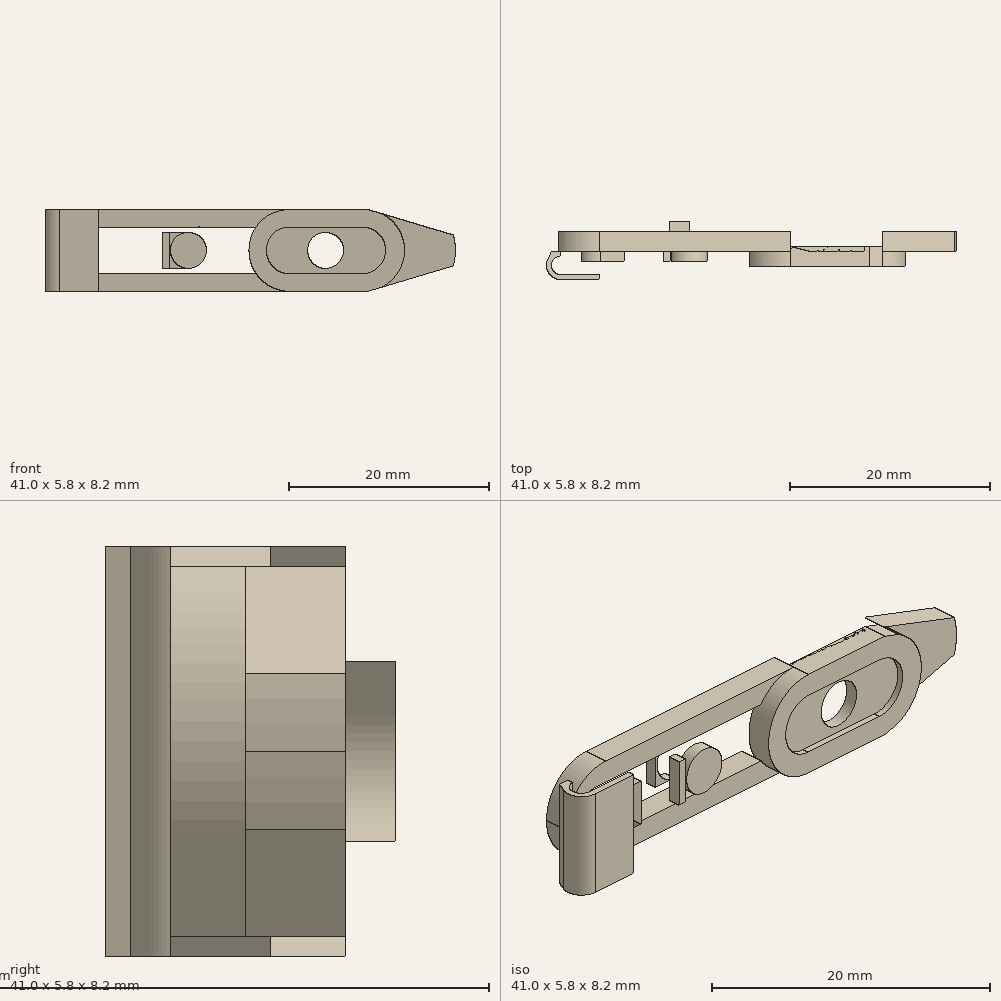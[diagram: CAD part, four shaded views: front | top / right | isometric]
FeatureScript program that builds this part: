
annotation { "Feature Type Name" : "Feature", "Feature Type Description" : "" }
export const myFeature = defineFeature(function(context is Context, id is Id, definition is map)
    precondition{}
    {
        {
            var Q0;
            Q0=qCreatedBy(makeId("Front.planeOp"),FACE);
            var sketch = newSketch(context, id + "F0", { "sketchPlane" : qUnion([Q0])});
            skLineSegment(sketch, "E0", {"start": v(24.15, -4.1) * mm, "end": v(24.15, 4.1) * mm});
            skLineSegment(sketch, "E1", {"start": v(24.15, 4.1) * mm, "end": v(-24.15, 4.1) * mm});
            skLineSegment(sketch, "E2", {"start": v(-24.15, 4.1) * mm, "end": v(-24.15, -4.1) * mm});
            skLineSegment(sketch, "E3", {"start": v(24.15, -4.1) * mm, "end": v(-24.15, -4.1) * mm});
            skLineSegment(sketch, "E4", {"start": v(-24.15, 0) * mm, "end": v(-24.15, 2.35) * mm});
            skLineSegment(sketch, "E5", {"start": v(-12.63, 2.35) * mm, "end": v(-1.7, 2.35) * mm});
            skLineSegment(sketch, "E6", {"start": v(7.64, 2.35) * mm, "end": v(14.81, 2.35) * mm});
            skLineSegment(sketch, "E7", {"start": v(-12.5, -2.35) * mm, "end": v(-1.7, -2.35) * mm});
            skLineSegment(sketch, "E8", {"start": v(7.5, -2.35) * mm, "end": v(14.81, -2.35) * mm});
            skArc(sketch, "E9", {"start": v(14.8, -0.1) * mm, "mid": v(14.9, 0) * mm, "end": v(14.8, 0.1) * mm});
            skArc(sketch, "E10", {"start": v(-12.63, 2.35) * mm, "mid": v(-14.91, -0.07) * mm, "end": v(-12.5, -2.35) * mm});
            skArc(sketch, "E11", {"start": v(14.85, 0.15) * mm, "mid": v(14.83, 0.16) * mm, "end": v(14.8, 0.16) * mm});
            skArc(sketch, "E12", {"start": v(14.96, 0) * mm, "mid": v(14.96, 0) * mm, "end": v(14.96, 0) * mm});
            skArc(sketch, "E13", {"start": v(14.8, -0.16) * mm, "mid": v(14.83, -0.16) * mm, "end": v(14.85, -0.15) * mm});
            skLineSegment(sketch, "E14", {"start": v(16.02, -3.91) * mm, "end": v(23.93, -1.56) * mm});
            skArc(sketch, "E15", {"start": v(23.66, -0.64) * mm, "mid": v(23.68, -0.62) * mm, "end": v(23.69, -0.6) * mm});
            skLineSegment(sketch, "E16", {"start": v(16.02, 3.91) * mm, "end": v(23.93, 1.56) * mm});
            skLineSegment(sketch, "E17", {"start": v(-14.84, 0) * mm, "end": v(-18.04, 0) * mm});
            skLineSegment(sketch, "E18", {"start": v(-13.4, -4) * mm, "end": v(-22.58, -1.95) * mm});
            skLineSegment(sketch, "E19", {"start": v(-22.58, -1.95) * mm, "end": v(-13.38, -4) * mm});
            skLineSegment(sketch, "E20", {"start": v(-22.48, 2.17) * mm, "end": v(-13.4, 4.01) * mm});
            skLineSegment(sketch, "E21", {"start": v(-13.02, 4.1) * mm, "end": v(-23.96, 1.87) * mm});
            skLineSegment(sketch, "E22", {"start": v(-12.94, -4.1) * mm, "end": v(-23.87, -1.67) * mm});
            skCircle(sketch, "E23", {"center": v(-11.6, 0) * mm, "radius": 1.8 * mm});
            skLineSegment(sketch, "E24", {"start": v(-14.84, 0) * mm, "end": v(0.66, 0) * mm});
            skArc(sketch, "E25", {"start": v(-1.42, -2.35) * mm, "mid": v(0.8, 0.14) * mm, "end": v(-1.7, 2.35) * mm});
            skLineSegment(sketch, "E26", {"start": v(0.66, 0) * mm, "end": v(-2.6, 0) * mm});
            skLineSegment(sketch, "E27", {"start": v(24.15, 0) * mm, "end": v(15.65, 0) * mm});
            skLineSegment(sketch, "E28", {"start": v(15.65, 0) * mm, "end": v(15.65, 0.9) * mm});
            skLineSegment(sketch, "E29", {"start": v(15.65, 0.9) * mm, "end": v(16.65, 0.9) * mm});
            skLineSegment(sketch, "E30", {"start": v(16.65, 0.9) * mm, "end": v(16.65, -0.9) * mm});
            skLineSegment(sketch, "E31", {"start": v(16.65, -0.9) * mm, "end": v(15.75, -0.9) * mm});
            skLineSegment(sketch, "E32", {"start": v(15.75, -0.9) * mm, "end": v(15.65, -0.9) * mm});
            skLineSegment(sketch, "E33", {"start": v(15.65, -0.9) * mm, "end": v(15.65, 0) * mm});
            skLineSegment(sketch, "E34", {"start": v(15.65, 0) * mm, "end": v(5.15, 0) * mm});
            skLineSegment(sketch, "E35", {"start": v(17.15, 0) * mm, "end": v(11.15, 0) * mm});
            skArc(sketch, "E36", {"start": v(11.85, -1.8) * mm, "mid": v(13.65, 0) * mm, "end": v(11.85, 1.8) * mm});
            skLineSegment(sketch, "E37", {"start": v(11.82, -0.07) * mm, "end": v(11.82, -0.07) * mm});
            skLineSegment(sketch, "E38", {"start": v(-24.15, 4.1) * mm, "end": v(-24.65, 4.1) * mm});
            skArc(sketch, "E39", {"start": v(-12.24, 1.8) * mm, "mid": v(-14.04, 0) * mm, "end": v(-12.24, -1.8) * mm});
            skArc(sketch, "E40", {"start": v(-1.95, -1.8) * mm, "mid": v(-0.15, 0) * mm, "end": v(-1.95, 1.8) * mm});
            skLineSegment(sketch, "E41", {"start": v(5.15, 0) * mm, "end": v(0.66, 0) * mm});
            skArc(sketch, "E42", {"start": v(7.64, 2.35) * mm, "mid": v(5.22, 0.07) * mm, "end": v(7.5, -2.35) * mm});
            skArc(sketch, "E43", {"start": v(14.81, -2.35) * mm, "mid": v(17.16, 0) * mm, "end": v(14.81, 2.35) * mm});
            skLineSegment(sketch, "E44", {"start": v(16.65, 0.9) * mm, "end": v(16.65, 1.45) * mm});
            skLineSegment(sketch, "E45", {"start": v(16.65, -0.9) * mm, "end": v(16.65, -1.45) * mm});
            skLineSegment(sketch, "E46", {"start": v(10.48, -0.07) * mm, "end": v(10.48, -0.07) * mm});
            skArc(sketch, "E47", {"start": v(10.45, 1.8) * mm, "mid": v(8.65, 0) * mm, "end": v(10.45, -1.8) * mm});
            skLineSegment(sketch, "E48", {"start": v(11.85, 1.8) * mm, "end": v(10.45, 1.8) * mm});
            skLineSegment(sketch, "E49", {"start": v(10.45, -1.8) * mm, "end": v(11.85, -1.8) * mm});
            skCircle(sketch, "E50", {"center": v(11.16, 0) * mm, "radius": 1.8 * mm});
            skLineSegment(sketch, "E51", {"start": v(-5.15, -1.8) * mm, "end": v(-5.15, 1.8) * mm});
            skArc(sketch, "E52", {"start": v(-1.95, -0.07) * mm, "mid": v(-1.88, 0) * mm, "end": v(-1.95, 0.07) * mm});
            skLineSegment(sketch, "E53", {"start": v(-1.95, 1.8) * mm, "end": v(-5.15, 1.8) * mm});
            skLineSegment(sketch, "E54", {"start": v(-1.95, -1.8) * mm, "end": v(-5.15, -1.8) * mm});
            skLineSegment(sketch, "E55", {"start": v(-4.54, -1.8) * mm, "end": v(-4.54, 1.8) * mm});
            skArc(sketch, "E56", {"start": v(-12.24, 0.07) * mm, "mid": v(-12.3, 0) * mm, "end": v(-12.24, -0.07) * mm});
            skLineSegment(sketch, "E57", {"start": v(-9.04, -1.8) * mm, "end": v(-9.04, 1.8) * mm});
            skLineSegment(sketch, "E58", {"start": v(-9.65, 1.8) * mm, "end": v(-9.65, -1.8) * mm});
            skLineSegment(sketch, "E59", {"start": v(-12.24, 1.8) * mm, "end": v(-9.04, 1.8) * mm});
            skLineSegment(sketch, "E60", {"start": v(-12.24, -1.8) * mm, "end": v(-9.04, -1.8) * mm});
            skArc(sketch, "E61", {"start": v(-7.84, -1.6) * mm, "mid": v(-7.09, -2.35) * mm, "end": v(-6.34, -1.6) * mm});
            skArc(sketch, "E62", {"start": v(-6.34, 1.6) * mm, "mid": v(-7.09, 2.35) * mm, "end": v(-7.84, 1.6) * mm});
            skLineSegment(sketch, "E63", {"start": v(-6.34, 1.6) * mm, "end": v(-6.34, -1.6) * mm});
            skLineSegment(sketch, "E64", {"start": v(-7.84, 1.6) * mm, "end": v(-7.84, -1.6) * mm});
            skLineSegment(sketch, "E65", {"start": v(-24.65, 0.68) * mm, "end": v(-24.65, -0.7) * mm});
            skArc(sketch, "E66", {"start": v(-24.65, -0.7) * mm, "mid": v(-24.43, -1.32) * mm, "end": v(-23.87, -1.67) * mm});
            skLineSegment(sketch, "E67", {"start": v(24.65, 0.6) * mm, "end": v(24.65, -0.6) * mm});
            skArc(sketch, "E68", {"start": v(23.69, 0.6) * mm, "mid": v(23.68, 0.62) * mm, "end": v(23.66, 0.64) * mm});
            skArc(sketch, "E69", {"start": v(-23.96, 1.87) * mm, "mid": v(-24.46, 1.37) * mm, "end": v(-24.65, 0.68) * mm});
            skArc(sketch, "E70", {"start": v(23.93, -1.56) * mm, "mid": v(24.15, 0) * mm, "end": v(23.93, 1.56) * mm});
            skLineSegment(sketch, "E71", {"start": v(24.15, 0) * mm, "end": v(24.65, 0) * mm});
            skArc(sketch, "E72", {"start": v(23.93, -1.56) * mm, "mid": v(24.65, 0) * mm, "end": v(23.93, 1.56) * mm});
            skLineSegment(sketch, "E73", {"start": v(23.93, 1.56) * mm, "end": v(15.4, 4.1) * mm});
            skLineSegment(sketch, "E74", {"start": v(23.93, -1.56) * mm, "end": v(15.4, -4.1) * mm});
            skCircle(sketch, "E75", {"center": v(-2.6, 0) * mm, "radius": 1.8 * mm});
            skArc(sketch, "E76", {"start": v(-2.6, -4.1) * mm, "mid": v(1.5, 0) * mm, "end": v(-2.6, 4.1) * mm});
            skArc(sketch, "E77", {"start": v(-11.6, 4.1) * mm, "mid": v(-14.5, 2.9) * mm, "end": v(-15.7, 0) * mm});
            skArc(sketch, "E78", {"start": v(-11.41, 4.1) * mm, "mid": v(-15.7, 0.1) * mm, "end": v(-11.6, -4.1) * mm});
            skArc(sketch, "E79", {"start": v(7.57, 4.1) * mm, "mid": v(3.47, 0) * mm, "end": v(7.57, -4.1) * mm});
            skArc(sketch, "E80", {"start": v(11.27, -1.78) * mm, "mid": v(11.27, -1.79) * mm, "end": v(11.28, -1.8) * mm});
            skArc(sketch, "E81.trimOffspring", {"start": v(11.27, 1.78) * mm, "mid": v(11.26, 1.79) * mm, "end": v(11.26, 1.8) * mm});
            skArc(sketch, "E82.trimOffspring", {"start": v(14.96, -4.1) * mm, "mid": v(19.06, 0) * mm, "end": v(14.96, 4.1) * mm});
            skArc(sketch, "E83.trimOffspring", {"start": v(11.26, -1.8) * mm, "mid": v(11.26, -1.79) * mm, "end": v(11.27, -1.78) * mm});
            skArc(sketch, "E84.trimOffspring", {"start": v(11.28, 1.8) * mm, "mid": v(11.27, 1.79) * mm, "end": v(11.27, 1.78) * mm});
            skLineSegment(sketch, "E85", {"start": v(7.64, 2.35) * mm, "end": v(-1.7, 2.35) * mm});
            skLineSegment(sketch, "E86", {"start": v(7.5, -2.35) * mm, "end": v(-1.7, -2.35) * mm});
            skSolve(sketch);
        }
        {
            var Q0;
            {var subQ0=sQuery(id+"F0.wireOp",EDGE,"E73");var subQ1=sQuery(id+"F0.wireOp",EDGE,"E1");var subQ2=makeQuery(id+"F0.imprint","INTERSECT",VERTEX,{"derivedFrom":[subQ1,subQ0]});Q0=makeQuery(id+"F0.imprint","IMPRINT",FACE,{"disambiguationData":[TD([[makeQuery(id+"F0.imprint","IMPRINT",EDGE,{"disambiguationData":[TD([[subQ2,-1.0]])],"derivedFrom":subQ1}),1.0]])]});}
            var Q1;
            {var subQ0=sQuery(id+"F0.wireOp",EDGE,"E1");var subQ1=makeQuery(id+"F0.imprint","INTERSECT",VERTEX,{"derivedFrom":[subQ0,sQuery(id+"F0.wireOp",EDGE,"E77")]});Q1=makeQuery(id+"F0.imprint","IMPRINT",FACE,{"disambiguationData":[TD([[makeQuery(id+"F0.imprint","IMPRINT",EDGE,{"disambiguationData":[TD([[subQ1,1.0]])],"derivedFrom":subQ0}),-1.0]])]});}
            var Q2;
            {var subQ0=sQuery(id+"F0.wireOp",EDGE,"E74");var subQ1=sQuery(id+"F0.wireOp",EDGE,"E3");var subQ2=makeQuery(id+"F0.imprint","INTERSECT",VERTEX,{"derivedFrom":[subQ1,subQ0]});Q2=makeQuery(id+"F0.imprint","IMPRINT",FACE,{"disambiguationData":[TD([[makeQuery(id+"F0.imprint","IMPRINT",EDGE,{"disambiguationData":[TD([[subQ2,-1.0]])],"derivedFrom":subQ1}),-1.0]])]});}
            var Q3;
            {var subQ0=sQuery(id+"F0.wireOp",EDGE,"E77");Q3=makeQuery(id+"F0.imprint","IMPRINT",FACE,{"disambiguationData":[TD([[makeQuery(id+"F0.imprint","IMPRINT",EDGE,{"derivedFrom":subQ0}),-1.0]])]});}
            var Q4;
            {var subQ1=sQuery(id+"F0.wireOp",EDGE,"E6");Q4=makeQuery(id+"F0.imprint","IMPRINT",FACE,{"disambiguationData":[TD([[makeQuery(id+"F0.imprint","IMPRINT",EDGE,{"derivedFrom":subQ1}),1.0]])]});}
            var Q5;
            {var subQ8=sQuery(id+"F0.wireOp",EDGE,"E77");Q5=makeQuery(id+"F0.imprint","IMPRINT",FACE,{"disambiguationData":[TD([[makeQuery(id+"F0.imprint","IMPRINT",EDGE,{"derivedFrom":subQ8}),1.0]])]});}
            var Q6;
            {var subQ10=sQuery(id+"F0.wireOp",EDGE,"E8");Q6=makeQuery(id+"F0.imprint","IMPRINT",FACE,{"disambiguationData":[TD([[makeQuery(id+"F0.imprint","IMPRINT",EDGE,{"derivedFrom":subQ10}),-1.0]])]});}
            var Q7;
            {var subQ6=sQuery(id+"F0.wireOp",EDGE,"E3");var subQ12=sQuery(id+"F0.wireOp",EDGE,"E76");var subQ13=makeQuery(id+"F0.imprint","INTERSECT",VERTEX,{"derivedFrom":[subQ6,subQ12]});Q7=makeQuery(id+"F0.imprint","IMPRINT",FACE,{"disambiguationData":[TD([[makeQuery(id+"F0.imprint","IMPRINT",EDGE,{"disambiguationData":[TD([[subQ13,-1.0]])],"derivedFrom":subQ6}),-1.0]])]});}
            var Q8;
            {var subQ16=sQuery(id+"F0.wireOp",EDGE,"E10");var subQ17=sQuery(id+"F0.wireOp",EDGE,"E5");var subQ18=makeQuery(id+"F0.imprint","INTERSECT",VERTEX,{"derivedFrom":[subQ17,subQ16]});Q8=makeQuery(id+"F0.imprint","IMPRINT",FACE,{"disambiguationData":[TD([[makeQuery(id+"F0.imprint","IMPRINT",EDGE,{"disambiguationData":[TD([[subQ18,-1.0]])],"derivedFrom":subQ17}),-1.0]])]});}
            var Q9;
            {var subQ3=sQuery(id+"F0.wireOp",EDGE,"E7");var subQ14=sQuery(id+"F0.wireOp",EDGE,"E10");var subQ15=makeQuery(id+"F0.imprint","INTERSECT",VERTEX,{"derivedFrom":[subQ3,subQ14]});Q9=makeQuery(id+"F0.imprint","IMPRINT",FACE,{"disambiguationData":[TD([[makeQuery(id+"F0.imprint","IMPRINT",EDGE,{"disambiguationData":[TD([[subQ15,-1.0]])],"derivedFrom":subQ3}),1.0]])]});}
            var Q10;
            {var subQ9=sQuery(id+"F0.wireOp",EDGE,"E25");var subQ10=sQuery(id+"F0.wireOp",EDGE,"E5");var subQ11=makeQuery(id+"F0.imprint","INTERSECT",VERTEX,{"derivedFrom":[subQ10,subQ9]});Q10=makeQuery(id+"F0.imprint","IMPRINT",FACE,{"disambiguationData":[TD([[makeQuery(id+"F0.imprint","IMPRINT",EDGE,{"disambiguationData":[TD([[subQ11,1.0]])],"derivedFrom":subQ10}),-1.0]])]});}
            var Q11;
            {var subQ11=sQuery(id+"F0.wireOp",EDGE,"E25");var subQ17=sQuery(id+"F0.wireOp",EDGE,"E7");var subQ18=makeQuery(id+"F0.imprint","INTERSECT",VERTEX,{"derivedFrom":[subQ17,subQ11]});Q11=makeQuery(id+"F0.imprint","IMPRINT",FACE,{"disambiguationData":[TD([[makeQuery(id+"F0.imprint","IMPRINT",EDGE,{"disambiguationData":[TD([[subQ18,1.0]])],"derivedFrom":subQ17}),1.0]])]});}
            var Q12;
            {var subQ1=sQuery(id+"F0.wireOp",EDGE,"E41");var subQ6=sQuery(id+"F0.wireOp",EDGE,"E34");var subQ9=makeQuery(id+"F0.imprint","INTERSECT",VERTEX,{"derivedFrom":[subQ6,subQ1]});Q12=makeQuery(id+"F0.imprint","IMPRINT",FACE,{"disambiguationData":[TD([[makeQuery(id+"F0.imprint","IMPRINT",EDGE,{"disambiguationData":[TD([[subQ9,1.0]])],"derivedFrom":subQ6}),-1.0]])]});}
            var Q13;
            {var subQ1=sQuery(id+"F0.wireOp",EDGE,"E41");var subQ5=sQuery(id+"F0.wireOp",EDGE,"E34");var subQ6=makeQuery(id+"F0.imprint","INTERSECT",VERTEX,{"derivedFrom":[subQ5,subQ1]});Q13=makeQuery(id+"F0.imprint","IMPRINT",FACE,{"disambiguationData":[TD([[makeQuery(id+"F0.imprint","IMPRINT",EDGE,{"disambiguationData":[TD([[subQ6,1.0]])],"derivedFrom":subQ5}),1.0]])]});}
            var Q14;
            {var subQ0=sQuery(id+"F0.wireOp",EDGE,"E41");var subQ1=sQuery(id+"F0.wireOp",EDGE,"E25");var subQ2=makeQuery(id+"F0.imprint","INTERSECT",VERTEX,{"derivedFrom":[subQ1,subQ0]});Q14=makeQuery(id+"F0.imprint","IMPRINT",FACE,{"disambiguationData":[TD([[makeQuery(id+"F0.imprint","IMPRINT",EDGE,{"disambiguationData":[TD([[subQ2,-1.0]])],"derivedFrom":subQ1}),-1.0]])]});}
            var Q15;
            {var subQ0=sQuery(id+"F0.wireOp",EDGE,"E86");var subQ1=sQuery(id+"F0.wireOp",EDGE,"E25");var subQ2=makeQuery(id+"F0.imprint","INTERSECT",VERTEX,{"derivedFrom":[subQ1,subQ0]});Q15=makeQuery(id+"F0.imprint","IMPRINT",FACE,{"disambiguationData":[TD([[makeQuery(id+"F0.imprint","IMPRINT",EDGE,{"disambiguationData":[TD([[subQ2,-1.0]])],"derivedFrom":subQ1}),-1.0]])]});}
            var Q16;
            {var subQ0=sQuery(id+"F0.wireOp",EDGE,"E85");var subQ1=sQuery(id+"F0.wireOp",EDGE,"E25");var subQ3=makeQuery(id+"F0.imprint","INTERSECT",VERTEX,{"derivedFrom":[subQ1,subQ0]});Q16=makeQuery(id+"F0.imprint","IMPRINT",FACE,{"disambiguationData":[TD([[makeQuery(id+"F0.imprint","IMPRINT",EDGE,{"disambiguationData":[TD([[subQ3,-1.0]])],"derivedFrom":subQ1}),1.0]])]});}
            var Q17;
            {var subQ15=sQuery(id+"F0.wireOp",EDGE,"E86");var subQ16=sQuery(id+"F0.wireOp",EDGE,"E7");var subQ17=makeQuery(id+"F0.imprint","INTERSECT",VERTEX,{"derivedFrom":[subQ16,subQ15]});Q17=makeQuery(id+"F0.imprint","IMPRINT",FACE,{"disambiguationData":[TD([[makeQuery(id+"F0.imprint","IMPRINT",EDGE,{"disambiguationData":[TD([[subQ17,1.0]])],"derivedFrom":subQ16}),1.0]])]});}
            extrude(context, id + "F1", {"entities" : qUnion([Q0, Q1, Q2, Q3, Q4, Q5, Q6, Q7, Q8, Q9, Q10, Q11, Q12, Q13, Q14, Q15, Q16, Q17]), "depth" : 3.5 * mm, "offsetDistance" : 25 * mm});
        }
        {
            var Q0;
            {var subQ1=sQuery(id+"F0.wireOp",EDGE,"E22");var subQ5=makeQuery(id+"F0.imprint","IMPRINT",VERTEX,{"disambiguationData":[OD(0.0)],"derivedFrom":subQ1});Q0=makeQuery(id+"F0.imprint","IMPRINT",FACE,{"disambiguationData":[TD([[makeQuery(id+"F0.imprint","IMPRINT",EDGE,{"disambiguationData":[TD([[subQ5,-1.0]])],"derivedFrom":subQ1}),-1.0]])]});}
            var Q1;
            {var subQ0=sQuery(id+"F0.wireOp",EDGE,"E76");var subQ1=sQuery(id+"F0.wireOp",EDGE,"E1");var subQ2=makeQuery(id+"F0.imprint","INTERSECT",VERTEX,{"derivedFrom":[subQ1,subQ0]});Q1=makeQuery(id+"F0.imprint","IMPRINT",FACE,{"disambiguationData":[TD([[makeQuery(id+"F0.imprint","IMPRINT",EDGE,{"disambiguationData":[TD([[subQ2,1.0]])],"derivedFrom":subQ1}),1.0]])]});}
            var Q2;
            {var subQ0=sQuery(id+"F0.wireOp",EDGE,"E76");var subQ1=sQuery(id+"F0.wireOp",EDGE,"E3");var subQ2=makeQuery(id+"F0.imprint","INTERSECT",VERTEX,{"derivedFrom":[subQ1,subQ0]});Q2=makeQuery(id+"F0.imprint","IMPRINT",FACE,{"disambiguationData":[TD([[makeQuery(id+"F0.imprint","IMPRINT",EDGE,{"disambiguationData":[TD([[subQ2,1.0]])],"derivedFrom":subQ1}),-1.0]])]});}
            var Q3;
            {var subQ3=sQuery(id+"F0.wireOp",EDGE,"E82.trimOffspring");var subQ7=sQuery(id+"F0.wireOp",EDGE,"E27");var subQ9=makeQuery(id+"F0.imprint","INTERSECT",VERTEX,{"derivedFrom":[subQ7,subQ3]});Q3=makeQuery(id+"F0.imprint","IMPRINT",FACE,{"disambiguationData":[TD([[makeQuery(id+"F0.imprint","IMPRINT",EDGE,{"disambiguationData":[TD([[subQ9,-1.0]])],"derivedFrom":subQ3}),-1.0]])]});}
            var Q4;
            {var subQ1=sQuery(id+"F0.wireOp",EDGE,"E27");var subQ3=sQuery(id+"F0.wireOp",EDGE,"E82.trimOffspring");var subQ4=makeQuery(id+"F0.imprint","INTERSECT",VERTEX,{"derivedFrom":[subQ1,subQ3]});Q4=makeQuery(id+"F0.imprint","IMPRINT",FACE,{"disambiguationData":[TD([[makeQuery(id+"F0.imprint","IMPRINT",EDGE,{"disambiguationData":[TD([[subQ4,1.0]])],"derivedFrom":subQ3}),-1.0]])]});}
            var Q5;
            {var subQ10=sQuery(id+"F0.wireOp",EDGE,"E77");Q5=makeQuery(id+"F0.imprint","IMPRINT",FACE,{"disambiguationData":[TD([[makeQuery(id+"F0.imprint","IMPRINT",EDGE,{"derivedFrom":subQ10}),1.0]])]});}
            var Q6;
            {var subQ9=sQuery(id+"F0.wireOp",EDGE,"E76");var subQ10=sQuery(id+"F0.wireOp",EDGE,"E3");var subQ11=makeQuery(id+"F0.imprint","INTERSECT",VERTEX,{"derivedFrom":[subQ10,subQ9]});Q6=makeQuery(id+"F0.imprint","IMPRINT",FACE,{"disambiguationData":[TD([[makeQuery(id+"F0.imprint","IMPRINT",EDGE,{"disambiguationData":[TD([[subQ11,-1.0]])],"derivedFrom":subQ10}),-1.0]])]});}
            var Q7;
            {var subQ5=sQuery(id+"F0.wireOp",EDGE,"E8");Q7=makeQuery(id+"F0.imprint","IMPRINT",FACE,{"disambiguationData":[TD([[makeQuery(id+"F0.imprint","IMPRINT",EDGE,{"derivedFrom":subQ5}),-1.0]])]});}
            var Q8;
            {var subQ8=sQuery(id+"F0.wireOp",EDGE,"E6");Q8=makeQuery(id+"F0.imprint","IMPRINT",FACE,{"disambiguationData":[TD([[makeQuery(id+"F0.imprint","IMPRINT",EDGE,{"derivedFrom":subQ8}),1.0]])]});}
            extrude(context, id + "F2", {"entities" : qUnion([Q0, Q1, Q2, Q3, Q4, Q5, Q6, Q7, Q8]), "depth" : 2 * mm, "offsetDistance" : 25 * mm});
        }
        {
            var Q0;
            Q0=makeQuery(id+"F1.opExtrude","CAP_FACE",FACE,{"disambiguationData":[OSD([sQuery(id+"F0.wireOp",EDGE,"E1"),sQuery(id+"F0.wireOp",EDGE,"E3"),sQuery(id+"F0.wireOp",EDGE,"E23"),sQuery(id+"F0.wireOp",EDGE,"E39"),sQuery(id+"F0.wireOp",EDGE,"E40"),sQuery(id+"F0.wireOp",EDGE,"E51"),sQuery(id+"F0.wireOp",EDGE,"E53"),sQuery(id+"F0.wireOp",EDGE,"E54"),sQuery(id+"F0.wireOp",EDGE,"E57"),sQuery(id+"F0.wireOp",EDGE,"E59"),sQuery(id+"F0.wireOp",EDGE,"E60"),sQuery(id+"F0.wireOp",EDGE,"E61"),sQuery(id+"F0.wireOp",EDGE,"E62"),sQuery(id+"F0.wireOp",EDGE,"E63"),sQuery(id+"F0.wireOp",EDGE,"E64"),sQuery(id+"F0.wireOp",EDGE,"E76"),sQuery(id+"F0.wireOp",EDGE,"E78")])],"isStart":false});
            cPlane(context, id + "F3", {"entities" : qUnion([Q0]), "cplaneType" : CPlaneType.OFFSET, "offset" : 0.5 * mm, "oppositeDirection" : true, "width" : 150 * mm, "height" : 150 * mm});
        }
        {
            var Q0;
            Q0=qCreatedBy(id+"F3.planeOp",FACE);
            var sketch = newSketch(context, id + "F4", { "sketchPlane" : qUnion([Q0])});
            skLineSegment(sketch, "E87.0", {"start": v(-9.04, -1.8) * mm, "end": v(-9.04, 1.8) * mm});
            skLineSegment(sketch, "E88.0", {"start": v(-12.24, 1.8) * mm, "end": v(-9.04, 1.8) * mm});
            skLineSegment(sketch, "E88.1", {"start": v(-12.24, -1.8) * mm, "end": v(-9.04, -1.8) * mm});
            skLineSegment(sketch, "E89.0", {"start": v(-9.65, 1.8) * mm, "end": v(-9.65, -1.8) * mm});
            skCircle(sketch, "E90.0", {"center": v(-11.6, 0) * mm, "radius": 1.8 * mm});
            skLineSegment(sketch, "E91", {"start": v(-7.09, 1.6) * mm, "end": v(-7.09, -1.6) * mm});
            skLineSegment(sketch, "E92.MirrorCS", {"start": v(-1.94, -1.8) * mm, "end": v(-5.14, -1.8) * mm});
            skLineSegment(sketch, "E93.MirrorCS", {"start": v(-5.14, -1.8) * mm, "end": v(-5.14, 1.8) * mm});
            skLineSegment(sketch, "E94.MirrorCS", {"start": v(-1.94, 1.8) * mm, "end": v(-5.14, 1.8) * mm});
            skLineSegment(sketch, "E95.MirrorCS", {"start": v(-4.53, 1.8) * mm, "end": v(-4.53, -1.8) * mm});
            skCircle(sketch, "E96.MirrorC", {"center": v(-2.58, 0) * mm, "radius": 1.8 * mm});
            skArc(sketch, "E97.0", {"start": v(7.64, 2.35) * mm, "mid": v(5.22, 0.07) * mm, "end": v(7.5, -2.35) * mm});
            skLineSegment(sketch, "E98.0", {"start": v(7.64, 2.35) * mm, "end": v(14.81, 2.35) * mm});
            skArc(sketch, "E98.1", {"start": v(14.81, -2.35) * mm, "mid": v(17.16, 0) * mm, "end": v(14.81, 2.35) * mm});
            skLineSegment(sketch, "E98.2", {"start": v(7.5, -2.35) * mm, "end": v(14.81, -2.35) * mm});
            skCircle(sketch, "E98.3", {"center": v(11.16, 0) * mm, "radius": 1.8 * mm});
            skSolve(sketch);
        }
        {
            var Q0;
            {var subQ0=sQuery(id+"F4.wireOp",EDGE,"E87.0");Q0=makeQuery(id+"F4.imprint","IMPRINT",FACE,{"disambiguationData":[TD([[makeQuery(id+"F4.imprint","IMPRINT",EDGE,{"derivedFrom":subQ0}),1.0]])]});}
            var Q1;
            {var subQ0=sQuery(id+"F4.wireOp",EDGE,"E89.0");Q1=makeQuery(id+"F4.imprint","IMPRINT",FACE,{"disambiguationData":[TD([[makeQuery(id+"F4.imprint","IMPRINT",EDGE,{"derivedFrom":subQ0}),-1.0]])]});}
            extrude(context, id + "F5", {"entities" : qUnion([Q0, Q1]), "operationType" : NewBodyOperationType.ADD, "oppositeDirection" : true, "depth" : 2 * mm, "offsetDistance" : 25 * mm});
        }
        {
            var Q0;
            {var subQ14=sQuery(id+"F0.wireOp",EDGE,"E8");Q0=makeQuery(id+"F0.imprint","IMPRINT",FACE,{"disambiguationData":[TD([[makeQuery(id+"F0.imprint","IMPRINT",EDGE,{"derivedFrom":subQ14}),1.0]])]});}
            var Q1;
            {var subQ10=sQuery(id+"F0.wireOp",EDGE,"E6");Q1=makeQuery(id+"F0.imprint","IMPRINT",FACE,{"disambiguationData":[TD([[makeQuery(id+"F0.imprint","IMPRINT",EDGE,{"derivedFrom":subQ10}),-1.0]])]});}
            var Q2;
            {var subQ4=sQuery(id+"F0.wireOp",EDGE,"E63");var subQ5=sQuery(id+"F0.wireOp",EDGE,"E24");var subQ6=makeQuery(id+"F0.imprint","INTERSECT",VERTEX,{"derivedFrom":[subQ5,subQ4]});Q2=makeQuery(id+"F0.imprint","IMPRINT",FACE,{"disambiguationData":[TD([[makeQuery(id+"F0.imprint","IMPRINT",EDGE,{"disambiguationData":[TD([[subQ6,-1.0]])],"derivedFrom":subQ5}),1.0]])]});}
            var Q3;
            {var subQ15=sQuery(id+"F0.wireOp",EDGE,"E86");var subQ16=sQuery(id+"F0.wireOp",EDGE,"E7");var subQ17=makeQuery(id+"F0.imprint","INTERSECT",VERTEX,{"derivedFrom":[subQ16,subQ15]});Q3=makeQuery(id+"F0.imprint","IMPRINT",FACE,{"disambiguationData":[TD([[makeQuery(id+"F0.imprint","IMPRINT",EDGE,{"disambiguationData":[TD([[subQ17,1.0]])],"derivedFrom":subQ16}),1.0]])]});}
            var Q4;
            {var subQ3=sQuery(id+"F0.wireOp",EDGE,"E7");var subQ17=sQuery(id+"F0.wireOp",EDGE,"E10");var subQ18=makeQuery(id+"F0.imprint","INTERSECT",VERTEX,{"derivedFrom":[subQ3,subQ17]});Q4=makeQuery(id+"F0.imprint","IMPRINT",FACE,{"disambiguationData":[TD([[makeQuery(id+"F0.imprint","IMPRINT",EDGE,{"disambiguationData":[TD([[subQ18,-1.0]])],"derivedFrom":subQ3}),1.0]])]});}
            var Q5;
            {var subQ15=sQuery(id+"F0.wireOp",EDGE,"E10");var subQ16=sQuery(id+"F0.wireOp",EDGE,"E5");var subQ17=makeQuery(id+"F0.imprint","INTERSECT",VERTEX,{"derivedFrom":[subQ16,subQ15]});Q5=makeQuery(id+"F0.imprint","IMPRINT",FACE,{"disambiguationData":[TD([[makeQuery(id+"F0.imprint","IMPRINT",EDGE,{"disambiguationData":[TD([[subQ17,-1.0]])],"derivedFrom":subQ16}),-1.0]])]});}
            var Q6;
            {var subQ0=sQuery(id+"F0.wireOp",EDGE,"E86");var subQ1=sQuery(id+"F0.wireOp",EDGE,"E25");var subQ2=makeQuery(id+"F0.imprint","INTERSECT",VERTEX,{"derivedFrom":[subQ1,subQ0]});Q6=makeQuery(id+"F0.imprint","IMPRINT",FACE,{"disambiguationData":[TD([[makeQuery(id+"F0.imprint","IMPRINT",EDGE,{"disambiguationData":[TD([[subQ2,-1.0]])],"derivedFrom":subQ1}),-1.0]])]});}
            var Q7;
            {var subQ0=sQuery(id+"F0.wireOp",EDGE,"E41");var subQ1=sQuery(id+"F0.wireOp",EDGE,"E25");var subQ2=makeQuery(id+"F0.imprint","INTERSECT",VERTEX,{"derivedFrom":[subQ1,subQ0]});Q7=makeQuery(id+"F0.imprint","IMPRINT",FACE,{"disambiguationData":[TD([[makeQuery(id+"F0.imprint","IMPRINT",EDGE,{"disambiguationData":[TD([[subQ2,-1.0]])],"derivedFrom":subQ1}),-1.0]])]});}
            var Q8;
            Q8=makeQuery(id+"F1.opExtrude","CAP_FACE",FACE,{"disambiguationData":[OSD([sQuery(id+"F0.wireOp",EDGE,"E1"),sQuery(id+"F0.wireOp",EDGE,"E3"),sQuery(id+"F0.wireOp",EDGE,"E6"),sQuery(id+"F0.wireOp",EDGE,"E8"),sQuery(id+"F0.wireOp",EDGE,"E42"),sQuery(id+"F0.wireOp",EDGE,"E43"),sQuery(id+"F0.wireOp",EDGE,"E73"),sQuery(id+"F0.wireOp",EDGE,"E74"),sQuery(id+"F0.wireOp",EDGE,"E79"),sQuery(id+"F0.wireOp",EDGE,"E82.trimOffspring")])],"isStart":true});
            var Q9;
            Q9=makeQuery(id+"F1.opExtrude","CAP_FACE",FACE,{"disambiguationData":[OSD([sQuery(id+"F0.wireOp",EDGE,"E1"),sQuery(id+"F0.wireOp",EDGE,"E3"),sQuery(id+"F0.wireOp",EDGE,"E6"),sQuery(id+"F0.wireOp",EDGE,"E8"),sQuery(id+"F0.wireOp",EDGE,"E42"),sQuery(id+"F0.wireOp",EDGE,"E43"),sQuery(id+"F0.wireOp",EDGE,"E73"),sQuery(id+"F0.wireOp",EDGE,"E74"),sQuery(id+"F0.wireOp",EDGE,"E79"),sQuery(id+"F0.wireOp",EDGE,"E82.trimOffspring")])],"isStart":false});
            extrude(context, id + "F6", {"entities" : qUnion([Q0, Q1, Q2, Q3, Q4, Q5, Q6, Q7, Q8, Q9]), "operationType" : NewBodyOperationType.REMOVE, "depth" : 1.5 * mm, "offsetDistance" : 25 * mm});
        }
        {
            var Q0;
            {var subQ0=sQuery(id+"F0.wireOp",EDGE,"E76");var subQ1=sQuery(id+"F0.wireOp",EDGE,"E1");var subQ2=makeQuery(id+"F0.imprint","INTERSECT",VERTEX,{"derivedFrom":[subQ1,subQ0]});Q0=makeQuery(id+"F0.imprint","IMPRINT",FACE,{"disambiguationData":[TD([[makeQuery(id+"F0.imprint","IMPRINT",EDGE,{"disambiguationData":[TD([[subQ2,1.0]])],"derivedFrom":subQ1}),1.0]])]});}
            cPlane(context, id + "F7", {"entities" : qUnion([Q0]), "cplaneType" : CPlaneType.OFFSET, "offset" : 0 * mm, "width" : 150 * mm, "height" : 150 * mm});
        }
        {
            var Q0;
            Q0=qCreatedBy(id+"F7.planeOp",FACE);
            var sketch = newSketch(context, id + "F8", { "sketchPlane" : qUnion([Q0])});
            skArc(sketch, "E99.0", {"start": v(-1.95, -1.8) * mm, "mid": v(-0.15, 0) * mm, "end": v(-1.95, 1.8) * mm});
            skArc(sketch, "E100.0", {"start": v(-1.42, -2.35) * mm, "mid": v(0.8, 0) * mm, "end": v(-1.42, 2.35) * mm});
            skLineSegment(sketch, "E100.1", {"start": v(-12.63, 2.35) * mm, "end": v(-1.7, 2.35) * mm});
            skLineSegment(sketch, "E100.2", {"start": v(-12.5, -2.35) * mm, "end": v(-1.7, -2.35) * mm});
            skArc(sketch, "E100.3", {"start": v(-12.63, 2.35) * mm, "mid": v(-14.91, -0.07) * mm, "end": v(-12.5, -2.35) * mm});
            skArc(sketch, "E100.4", {"start": v(7.64, 2.35) * mm, "mid": v(5.22, 0.07) * mm, "end": v(7.5, -2.35) * mm});
            skLineSegment(sketch, "E100.5", {"start": v(7.64, 2.35) * mm, "end": v(14.81, 2.35) * mm});
            skArc(sketch, "E100.6", {"start": v(14.81, -2.35) * mm, "mid": v(17.16, 0) * mm, "end": v(14.81, 2.35) * mm});
            skLineSegment(sketch, "E100.7", {"start": v(7.5, -2.35) * mm, "end": v(14.81, -2.35) * mm});
            skLineSegment(sketch, "E101.0", {"start": v(7.64, 2.35) * mm, "end": v(-1.42, 2.35) * mm});
            skPoint(sketch, "E102.orphan", {"position": v(-1.7, 2.35) * mm});
            skSolve(sketch);
        }
        {
            var Q0;
            Q0 = qSketchRegion(id + "F8", true);
            extrude(context, id + "F9", {"entities" : qUnion([Q0]), "operationType" : NewBodyOperationType.REMOVE, "depth" : 1.5 * mm, "offsetDistance" : 25 * mm});
        }
        {
            var Q0;
            {var subQ1=sQuery(id+"F0.wireOp",EDGE,"E41");var subQ6=sQuery(id+"F0.wireOp",EDGE,"E34");var subQ9=makeQuery(id+"F0.imprint","INTERSECT",VERTEX,{"derivedFrom":[subQ6,subQ1]});Q0=makeQuery(id+"F0.imprint","IMPRINT",FACE,{"disambiguationData":[TD([[makeQuery(id+"F0.imprint","IMPRINT",EDGE,{"disambiguationData":[TD([[subQ9,1.0]])],"derivedFrom":subQ6}),-1.0]])]});}
            var Q1;
            {var subQ1=sQuery(id+"F0.wireOp",EDGE,"E41");var subQ5=sQuery(id+"F0.wireOp",EDGE,"E34");var subQ6=makeQuery(id+"F0.imprint","INTERSECT",VERTEX,{"derivedFrom":[subQ5,subQ1]});Q1=makeQuery(id+"F0.imprint","IMPRINT",FACE,{"disambiguationData":[TD([[makeQuery(id+"F0.imprint","IMPRINT",EDGE,{"disambiguationData":[TD([[subQ6,1.0]])],"derivedFrom":subQ5}),1.0]])]});}
            extrude(context, id + "F10", {"entities" : qUnion([Q0, Q1]), "operationType" : NewBodyOperationType.REMOVE, "depth" : 1.5 * mm, "offsetDistance" : 25 * mm});
        }
        {
            var Q0;
            Q0 = qSketchRegion(id + "F4", true);
            var Q1;
            {var subQ0=sQuery(id+"F0.wireOp",EDGE,"E26");var subQ3=makeQuery(id+"F0.imprint","IMPRINT",VERTEX,{"derivedFrom":subQ0});Q1=makeQuery(id+"F0.imprint","IMPRINT",FACE,{"disambiguationData":[TD([[makeQuery(id+"F0.imprint","IMPRINT",EDGE,{"disambiguationData":[TD([[subQ3,1.0]])],"derivedFrom":subQ0}),-1.0]])]});}
            var Q2;
            {var subQ0=sQuery(id+"F0.wireOp",EDGE,"E55");var subQ1=sQuery(id+"F0.wireOp",EDGE,"E24");var subQ2=makeQuery(id+"F0.imprint","INTERSECT",VERTEX,{"derivedFrom":[subQ1,subQ0]});Q2=makeQuery(id+"F0.imprint","IMPRINT",FACE,{"disambiguationData":[TD([[makeQuery(id+"F0.imprint","IMPRINT",EDGE,{"disambiguationData":[TD([[subQ2,-1.0]])],"derivedFrom":subQ1}),1.0]])]});}
            var Q3;
            {var subQ0=sQuery(id+"F0.wireOp",EDGE,"E40");var subQ1=sQuery(id+"F0.wireOp",EDGE,"E26");var subQ2=makeQuery(id+"F0.imprint","INTERSECT",VERTEX,{"derivedFrom":[subQ1,subQ0]});Q3=makeQuery(id+"F0.imprint","IMPRINT",FACE,{"disambiguationData":[TD([[makeQuery(id+"F0.imprint","IMPRINT",EDGE,{"disambiguationData":[TD([[subQ2,-1.0]])],"derivedFrom":subQ1}),-1.0]])]});}
            var Q4;
            {var subQ0=sQuery(id+"F0.wireOp",EDGE,"E40");var subQ1=sQuery(id+"F0.wireOp",EDGE,"E26");var subQ2=makeQuery(id+"F0.imprint","INTERSECT",VERTEX,{"derivedFrom":[subQ1,subQ0]});Q4=makeQuery(id+"F0.imprint","IMPRINT",FACE,{"disambiguationData":[TD([[makeQuery(id+"F0.imprint","IMPRINT",EDGE,{"disambiguationData":[TD([[subQ2,-1.0]])],"derivedFrom":subQ1}),1.0]])]});}
            var Q5;
            {var subQ0=sQuery(id+"F0.wireOp",EDGE,"E55");var subQ1=sQuery(id+"F0.wireOp",EDGE,"E24");var subQ2=makeQuery(id+"F0.imprint","INTERSECT",VERTEX,{"derivedFrom":[subQ1,subQ0]});Q5=makeQuery(id+"F0.imprint","IMPRINT",FACE,{"disambiguationData":[TD([[makeQuery(id+"F0.imprint","IMPRINT",EDGE,{"disambiguationData":[TD([[subQ2,-1.0]])],"derivedFrom":subQ1}),-1.0]])]});}
            var Q6;
            {var subQ4=sQuery(id+"F0.wireOp",EDGE,"E26");var subQ6=makeQuery(id+"F0.imprint","IMPRINT",VERTEX,{"derivedFrom":subQ4});Q6=makeQuery(id+"F0.imprint","IMPRINT",FACE,{"disambiguationData":[TD([[makeQuery(id+"F0.imprint","IMPRINT",EDGE,{"disambiguationData":[TD([[subQ6,1.0]])],"derivedFrom":subQ4}),1.0]])]});}
            extrude(context, id + "F11", {"entities" : qUnion([Q0, Q1, Q2, Q3, Q4, Q5, Q6]), "oppositeDirection" : true, "depth" : 1 * mm, "offsetDistance" : 25 * mm});
        }
        {
            var Q0;
            Q0=sQuery(id+"F0.wireOp",EDGE,"E23");
            extrude(context, id + "F12", {"bodyType" : ToolBodyType.SURFACE, "surfaceEntities" : qUnion([Q0]), "depth" : 4.8 * mm, "offsetDistance" : 25 * mm});
        }
        {
            var Q0;
            Q0=makeQuery(id+"F1.opExtrude","SWEPT_BODY",BODY,{"disambiguationData":[OSD([sQuery(id+"F0.wireOp",EDGE,"E1"),sQuery(id+"F0.wireOp",EDGE,"E3"),sQuery(id+"F0.wireOp",EDGE,"E23"),sQuery(id+"F0.wireOp",EDGE,"E39"),sQuery(id+"F0.wireOp",EDGE,"E40"),sQuery(id+"F0.wireOp",EDGE,"E51"),sQuery(id+"F0.wireOp",EDGE,"E53"),sQuery(id+"F0.wireOp",EDGE,"E54"),sQuery(id+"F0.wireOp",EDGE,"E57"),sQuery(id+"F0.wireOp",EDGE,"E59"),sQuery(id+"F0.wireOp",EDGE,"E60"),sQuery(id+"F0.wireOp",EDGE,"E61"),sQuery(id+"F0.wireOp",EDGE,"E62"),sQuery(id+"F0.wireOp",EDGE,"E63"),sQuery(id+"F0.wireOp",EDGE,"E64"),sQuery(id+"F0.wireOp",EDGE,"E76"),sQuery(id+"F0.wireOp",EDGE,"E78")])]});
            deleteBodies(context, id + "F13", {"entities" : qUnion([Q0])});
        }
        {
            var Q0;
            Q0=makeQuery(id+"F2.opExtrude","SWEPT_FACE",FACE,{"disambiguationData":[OSD([sQuery(id+"F0.wireOp",EDGE,"E3")])]});
            var sketch = newSketch(context, id + "F14", { "sketchPlane" : qUnion([Q0])});
            skLineSegment(sketch, "E103", {"start": v(-11.6, 2) * mm, "end": v(-11.6, 0) * mm});
            skLineSegment(sketch, "E104", {"start": v(-11.6, 2) * mm, "end": v(-13.4, 2) * mm});
            skLineSegment(sketch, "E105", {"start": v(-13.4, 2) * mm, "end": v(-13.4, 4.8) * mm});
            skLineSegment(sketch, "E106", {"start": v(-14.03, 2) * mm, "end": v(-16.4, 2) * mm});
            skLineSegment(sketch, "E107", {"start": v(-16.4, 2) * mm, "end": v(-16.4, 2.33) * mm});
            skArc(sketch, "E108", {"start": v(-15.5, 4.3) * mm, "mid": v(-16.4, 3.4) * mm, "end": v(-15.5, 2.5) * mm});
            skLineSegment(sketch, "E109", {"start": v(-15.5, 4.8) * mm, "end": v(-15.22, 4.8) * mm});
            skArc(sketch, "E110", {"start": v(-15.5, 4.8) * mm, "mid": v(-16.9, 3.4) * mm, "end": v(-15.5, 2) * mm});
            skPoint(sketch, "E111.endSnap0", {"position": v(-15.8, 4.8) * mm});
            skLineSegment(sketch, "E112", {"start": v(-15.5, 4.8) * mm, "end": v(-13.4, 4.8) * mm});
            skLineSegment(sketch, "E113", {"start": v(-15.5, 4.3) * mm, "end": v(-13.4, 4.3) * mm});
            skLineSegment(sketch, "E114", {"start": v(-15.5, 2.5) * mm, "end": v(-14.03, 2.5) * mm});
            skPoint(sketch, "E115.orphan", {"position": v(-16.4, 4.8) * mm});
            skLineSegment(sketch, "E116", {"start": v(-11.6, 2) * mm, "end": v(-11.6, 4.8) * mm});
            skLineSegment(sketch, "E117", {"start": v(-11.6, 4.8) * mm, "end": v(-13.4, 4.8) * mm});
            skLineSegment(sketch, "E118", {"start": v(-13.4, 4.3) * mm, "end": v(-11.6, 4.3) * mm});
            skLineSegment(sketch, "E119.bottom", {"start": v(-15.5, 2) * mm, "end": v(-14.03, 2) * mm});
            skLineSegment(sketch, "E119.left", {"start": v(-15.5, 2) * mm, "end": v(-15.5, 2.5) * mm});
            skLineSegment(sketch, "E119.right", {"start": v(-14.03, 2) * mm, "end": v(-14.03, 2.5) * mm});
            skSolve(sketch);
        }
        {
            var Q0;
            {var subQ0=sQuery(id+"F14.wireOp",EDGE,"E107");Q0=makeQuery(id+"F14.imprint","IMPRINT",FACE,{"disambiguationData":[TD([[makeQuery(id+"F14.imprint","IMPRINT",EDGE,{"derivedFrom":subQ0}),-1.0]])]});}
            var Q1;
            Q1=makeQuery(id+"F14.imprint","IMPRINT",FACE,{"disambiguationData":[TD([[makeQuery(id+"F14.imprint","IMPRINT",EDGE,{"derivedFrom":sQuery(id+"F14.wireOp",EDGE,"E108")}),-1.0]])]});
            var Q2;
            {var subQ0=sQuery(id+"F14.wireOp",EDGE,"E117");Q2=makeQuery(id+"F14.imprint","IMPRINT",FACE,{"disambiguationData":[TD([[makeQuery(id+"F14.imprint","IMPRINT",EDGE,{"derivedFrom":subQ0}),1.0]])]});}
            extrude(context, id + "F15", {"entities" : qUnion([Q0, Q1, Q2]), "oppositeDirection" : true, "depth" : 8.2 * mm, "offsetDistance" : 25 * mm});
        }
        {
            var Q0;
            Q0=makeQuery(id+"F15.opExtrude","SWEPT_EDGE",EDGE,{"disambiguationData":[OSD([sQuery(id+"F14.wireOp",EDGE,"E107"),sQuery(id+"F14.wireOp",EDGE,"E110")])]});
            fillet(context, id + "F16", {"entities" : qUnion([Q0]), "radius" : 5 * mm, "tangentPropagation" : true, "allowEdgeOverflow" : false});
        }
    });
